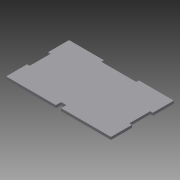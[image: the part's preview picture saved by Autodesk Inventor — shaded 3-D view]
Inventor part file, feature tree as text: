
AUTODESK INVENTOR PART (.ipt)
format: ipt  version: 2013 (Build 170138000, 138)  size: 107,008 bytes
history: native  units: mm
features: extrude x3, sketch x3
ambient origin geometry x8: Origin, YZ Plane, XZ Plane, XY Plane, X Axis, Y Axis, Z Axis, Center Point
bodies: Solid1 (feature_tree)
feature tree (6):
  extrude  "Extrusion1"  Depth=76.2mm
  extrude  "Extrusion2"  TaperAngle=0.0deg  [1 undecoded]
  extrude  "Extrusion3"  Depth=25.4mm
  sketch  "Sketch1"  dims[d0=127.0mm d1=76.2mm]
  sketch  "Sketch4"  dims[d2=3.1496mm d3=0.0mm]
  sketch  "Sketch5"  dims[d7=3.1496mm d8=25.4mm d9=25.4mm d10=3.1496mm d11=25.4mm d12=25.4mm d13=42.333333mm d14=3.1496mm d15=42.333333mm d16=3.1496mm d17=0.0mm d18=6.35mm d19=6.35mm d20=60.325mm d21=3.1496mm d22=0.0mm]
note: 1 required parameter value undecoded (feature->parameter linkage not recoverable at this tier; creation-order binding heuristic only, values carry confidence <= 0.55)
